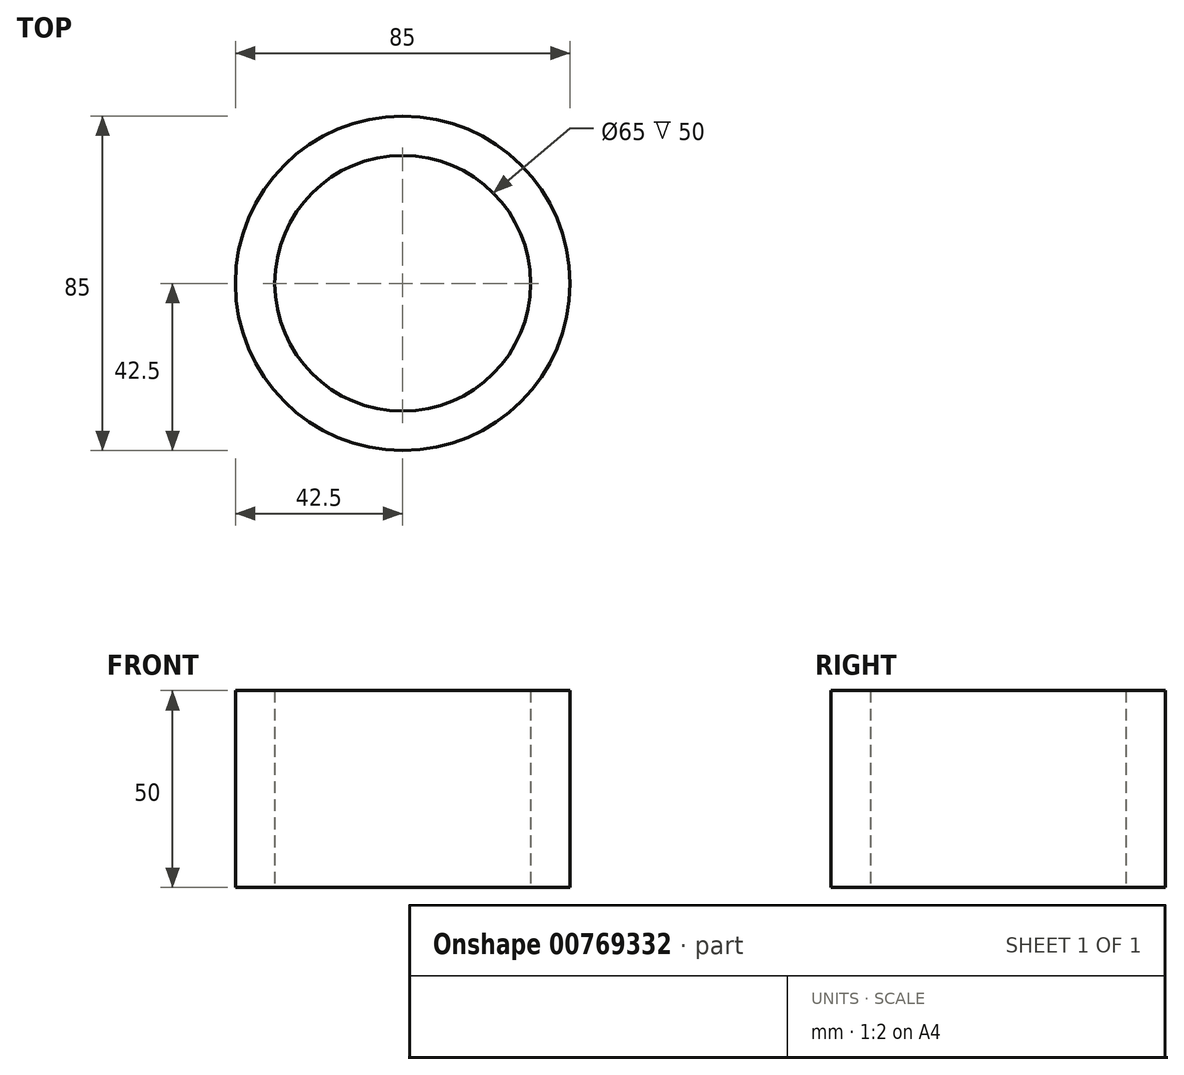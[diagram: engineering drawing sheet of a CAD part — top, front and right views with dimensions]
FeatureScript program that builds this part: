
annotation { "Feature Type Name" : "Feature", "Feature Type Description" : "" }
export const myFeature = defineFeature(function(context is Context, id is Id, definition is map)
    precondition{}
    {
        {
            var Q0;
            Q0=qCreatedBy(makeId("Top.planeOp"),FACE);
            var sketch = newSketch(context, id + "F0", { "sketchPlane" : qUnion([Q0])});
            skCircle(sketch, "E0", {"center": v(0, 0) * mm, "radius": 32.5 * mm});
            skCircle(sketch, "E1", {"center": v(0, 0) * mm, "radius": 42.5 * mm});
            skSolve(sketch);
        }
        {
            var Q0;
            Q0=makeQuery(id+"F0.imprint","IMPRINT",FACE,{"disambiguationData":[TD([[makeQuery(id+"F0.imprint","IMPRINT",EDGE,{"derivedFrom":sQuery(id+"F0.wireOp",EDGE,"E0")}),-1.0]])]});
            extrude(context, id + "F1", {"entities" : qUnion([Q0]), "depth" : 50 * mm, "offsetDistance" : 25 * mm});
        }
    });
